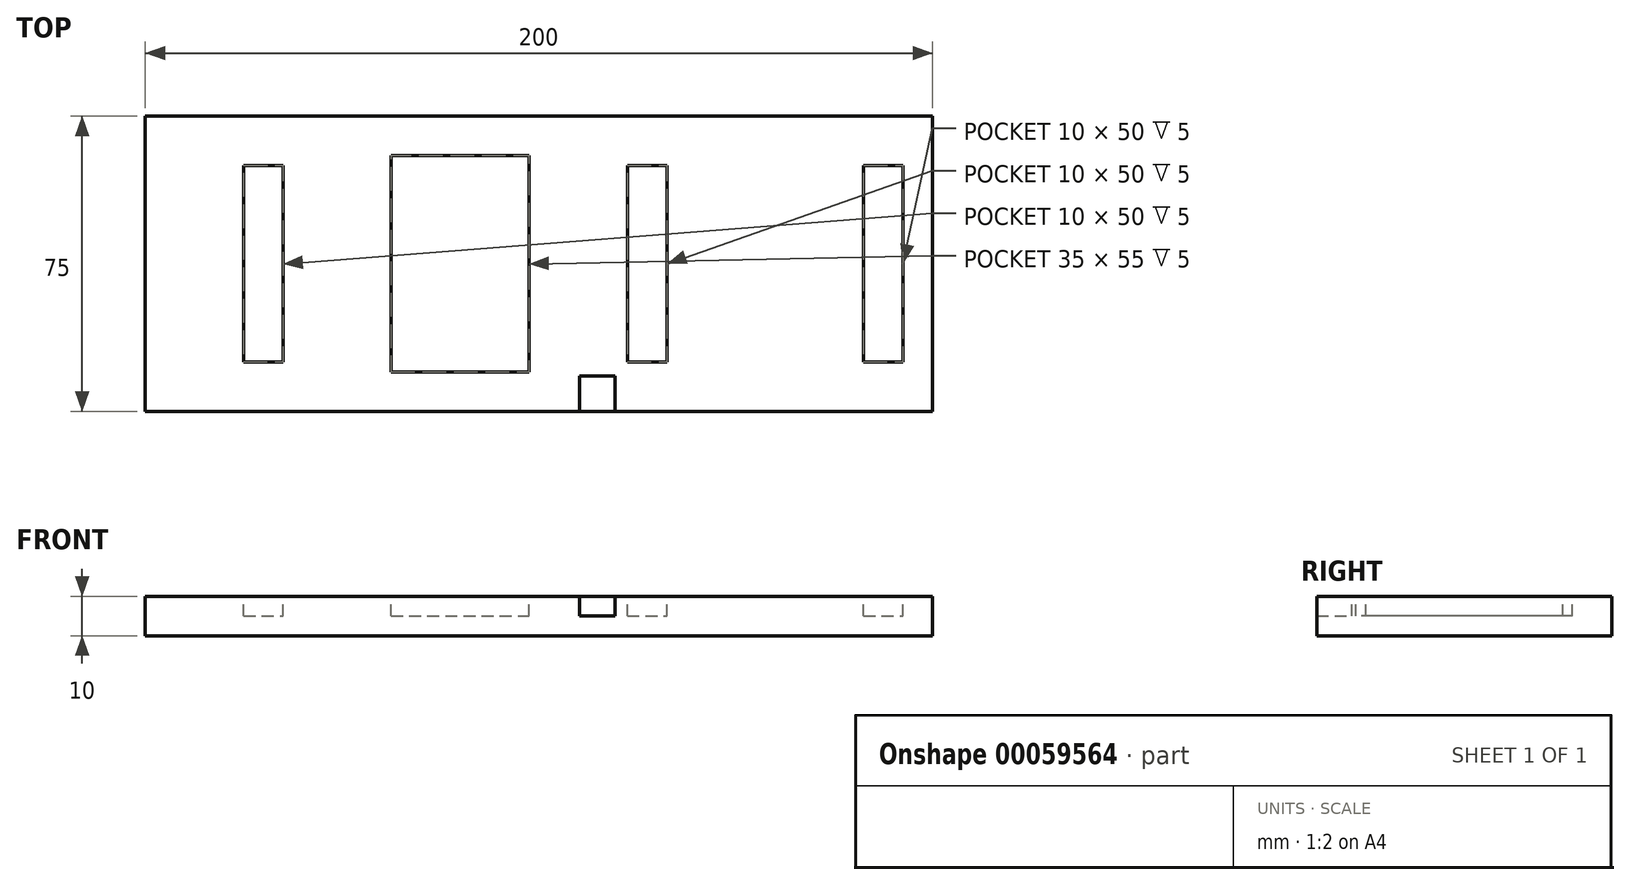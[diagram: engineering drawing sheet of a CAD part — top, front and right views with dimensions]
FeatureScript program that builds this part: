
annotation { "Feature Type Name" : "Feature", "Feature Type Description" : "" }
export const myFeature = defineFeature(function(context is Context, id is Id, definition is map)
    precondition{}
    {
        {
            var Q0;
            Q0=qCreatedBy(makeId("Top.planeOp"),FACE);
            var sketch = newSketch(context, id + "F0", { "sketchPlane" : qUnion([Q0])});
            skLineSegment(sketch, "E0.rect.bottom", {"start": v(-100, 37.5) * mm, "end": v(100, 37.5) * mm});
            skLineSegment(sketch, "E0.rect.top", {"start": v(-100, -37.5) * mm, "end": v(100, -37.5) * mm});
            skLineSegment(sketch, "E0.rect.left", {"start": v(-100, 37.5) * mm, "end": v(-100, -37.5) * mm});
            skLineSegment(sketch, "E0.rect.right", {"start": v(100, 37.5) * mm, "end": v(100, -37.5) * mm});
            skPoint(sketch, "E0.rect.middle", {"position": v(0, 0) * mm});
            skSolve(sketch);
        }
        {
            var Q0;
            Q0=makeQuery(id+"F0.imprint","IMPRINT",FACE,{"disambiguationData":[TD([[makeQuery(id+"F0.imprint","IMPRINT",EDGE,{"derivedFrom":sQuery(id+"F0.wireOp",EDGE,"E0.rect.bottom")}),-1.0]])]});
            extrude(context, id + "F1", {"entities" : qUnion([Q0]), "depth" : 10 * mm});
        }
        {
            var Q0;
            Q0=makeQuery(id+"F1.opExtrude","CAP_FACE",FACE,{"disambiguationData":[OSD([sQuery(id+"F0.wireOp",EDGE,"E0.rect.bottom"),sQuery(id+"F0.wireOp",EDGE,"E0.rect.top"),sQuery(id+"F0.wireOp",EDGE,"E0.rect.left"),sQuery(id+"F0.wireOp",EDGE,"E0.rect.right")])],"isStart":false});
            var sketch = newSketch(context, id + "F2", { "sketchPlane" : qUnion([Q0])});
            skLineSegment(sketch, "E1.bottom", {"start": v(-75, 25) * mm, "end": v(-65, 25) * mm});
            skLineSegment(sketch, "E1.top", {"start": v(-75, -25) * mm, "end": v(-65, -25) * mm});
            skLineSegment(sketch, "E1.left", {"start": v(-75, 25) * mm, "end": v(-75, -25) * mm});
            skLineSegment(sketch, "E1.right", {"start": v(-65, 25) * mm, "end": v(-65, -25) * mm});
            skPoint(sketch, "E1.middle", {"position": v(-70, 0) * mm});
            skLineSegment(sketch, "E2.bottom", {"start": v(22.5, 25) * mm, "end": v(32.5, 25) * mm});
            skLineSegment(sketch, "E2.top", {"start": v(22.5, -25) * mm, "end": v(32.5, -25) * mm});
            skLineSegment(sketch, "E2.left", {"start": v(22.5, 25) * mm, "end": v(22.5, -25) * mm});
            skLineSegment(sketch, "E2.right", {"start": v(32.5, 25) * mm, "end": v(32.5, -25) * mm});
            skPoint(sketch, "E2.middle", {"position": v(27.5, 0) * mm});
            skLineSegment(sketch, "E3", {"start": v(-100, 0) * mm, "end": v(100, 0) * mm, "construction": true});
            skLineSegment(sketch, "E4.bottom", {"start": v(82.5, 25) * mm, "end": v(92.5, 25) * mm});
            skLineSegment(sketch, "E4.top", {"start": v(82.5, -25) * mm, "end": v(92.5, -25) * mm});
            skLineSegment(sketch, "E4.left", {"start": v(82.5, 25) * mm, "end": v(82.5, -25) * mm});
            skLineSegment(sketch, "E4.right", {"start": v(92.5, 25) * mm, "end": v(92.5, -25) * mm});
            skPoint(sketch, "E4.middle", {"position": v(87.5, 0) * mm});
            skSolve(sketch);
        }
        {
            var Q0;
            Q0 = qSketchRegion(id + "F2", true);
            extrude(context, id + "F3", {"entities" : qUnion([Q0]), "operationType" : NewBodyOperationType.REMOVE, "oppositeDirection" : true, "depth" : 5 * mm});
        }
        {
            var Q0;
            Q0=makeQuery(id+"F1.opExtrude","CAP_FACE",FACE,{"disambiguationData":[OSD([sQuery(id+"F0.wireOp",EDGE,"E0.rect.bottom"),sQuery(id+"F0.wireOp",EDGE,"E0.rect.top"),sQuery(id+"F0.wireOp",EDGE,"E0.rect.left"),sQuery(id+"F0.wireOp",EDGE,"E0.rect.right")])],"isStart":false});
            var sketch = newSketch(context, id + "F4", { "sketchPlane" : qUnion([Q0])});
            skLineSegment(sketch, "E5.bottom", {"start": v(-37.54, 27.5) * mm, "end": v(-2.54, 27.5) * mm});
            skLineSegment(sketch, "E5.top", {"start": v(-37.54, -27.5) * mm, "end": v(-2.54, -27.5) * mm});
            skLineSegment(sketch, "E5.left", {"start": v(-37.54, 27.5) * mm, "end": v(-37.54, -27.5) * mm});
            skLineSegment(sketch, "E5.right", {"start": v(-2.54, 27.5) * mm, "end": v(-2.54, -27.5) * mm});
            skPoint(sketch, "E5.middle", {"position": v(-20.04, 0) * mm});
            skPoint(sketch, "E5.middle.positionSnap0", {"position": v(-65, 0) * mm});
            skPoint(sketch, "E5.centerSnap0", {"position": v(-65, 0) * mm});
            skLineSegment(sketch, "E6.bottom", {"start": v(10.38, -37.5) * mm, "end": v(19.38, -37.5) * mm});
            skLineSegment(sketch, "E6.top", {"start": v(10.38, -28.5) * mm, "end": v(19.38, -28.5) * mm});
            skLineSegment(sketch, "E6.left", {"start": v(10.38, -37.5) * mm, "end": v(10.38, -28.5) * mm});
            skLineSegment(sketch, "E6.right", {"start": v(19.38, -37.5) * mm, "end": v(19.38, -28.5) * mm});
            skSolve(sketch);
        }
        {
            var Q0;
            Q0 = qSketchRegion(id + "F4", true);
            extrude(context, id + "F5", {"entities" : qUnion([Q0]), "operationType" : NewBodyOperationType.REMOVE, "oppositeDirection" : true, "depth" : 5 * mm});
        }
    });
